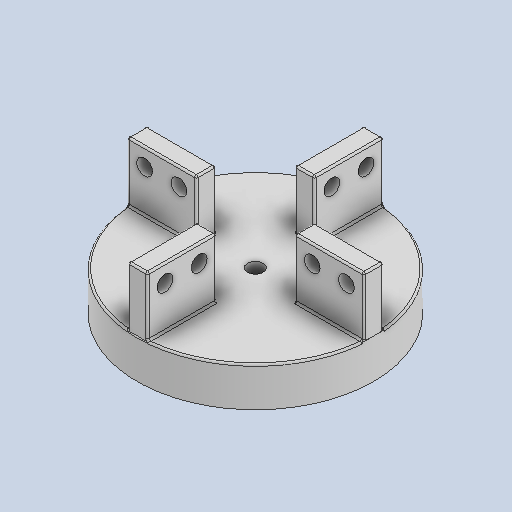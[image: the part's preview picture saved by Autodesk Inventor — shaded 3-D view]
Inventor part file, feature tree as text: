
AUTODESK INVENTOR PART (.ipt)
format: ipt  version: 2022 (Build 260153000, 153)  size: 440,320 bytes
history: native  units: mm
features: extrude x5, sketch x5, fillet x1
ambient origin geometry x8: Origin, YZ Plane, XZ Plane, XY Plane, X Axis, Y Axis, Z Axis, Center Point
bodies: Solid1 (feature_tree)
feature tree (11):
  extrude  "Extrusion1"  Depth=2.66mm
  extrude  "Extrusion2"  Depth=11.66mm
  fillet  "Fillet1"  Radius=1.65mm
  extrude  "Extrusion3"  Depth=1.65mm
  extrude  "Extrusion4"  Depth=1.65mm
  extrude  "Extrusion5"  Depth=10.0mm
  sketch  "Sketch1"  dims[d0=40.0mm d1=2.66mm]
  sketch  "Sketch2"  dims[d2=6.66mm d3=0.0mm d4=11.66mm d5=1.65mm]
  sketch  "Sketch3"  dims[d6=11.66mm d7=1.65mm]
  sketch  "Sketch4"  dims[d8=11.66mm d9=1.65mm]
  sketch  "Sketch5"  dims[d10=11.66mm d11=11.66mm d12=1.65mm d13=1.65mm d14=10.0mm d15=0.0mm d16=0.3mm d17=11.06mm d18=2.66mm d19=2.66mm d20=5.8mm d21=2.66mm d22=10.0mm d23=0.0mm d24=2.66mm d25=2.9mm d26=5.8mm d27=2.66mm d28=2.66mm d29=10.0mm d30=0.0mm d31=2.66mm d32=2.9mm d33=5.8mm d34=2.66mm d35=2.9mm d36=5.8mm d37=2.66mm d38=2.66mm d39=10.0mm d40=0.0mm]
